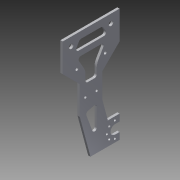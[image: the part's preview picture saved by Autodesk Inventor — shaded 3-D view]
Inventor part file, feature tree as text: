
AUTODESK INVENTOR PART (.ipt)
format: ipt  version: 2013 (Build 170138000, 138)  size: 268,288 bytes
history: native  units: mm
features: sketch x8, extrude x6, fillet x3, hole x2, other x1, pattern_circular x1
ambient origin geometry x8: Origin, YZ Plane, XZ Plane, XY Plane, X Axis, Y Axis, Z Axis, Center Point
feature tree (21):
  other  "ソリッド1"
  extrude  "押し出し1"  Depth=50.0mm
  extrude  "押し出し2"  Depth=100.0mm
  extrude  "押し出し5"  Depth=50.0mm
  hole  "穴1"  [1 undecoded]
  pattern_circular  "円形状パターン2"  [2 undecoded]
  hole  "穴2"  [1 undecoded]
  extrude  "押し出し7"  TaperAngle=135.0deg  [1 undecoded]
  extrude  "押し出し8"  Depth=25.0mm
  fillet  "フィレット1"  Radius=25.0mm
  fillet  "フィレット2"  Radius=50.0mm
  extrude  "押し出し9"  TaperAngle=165.0deg  [1 undecoded]
  fillet  "フィレット3"  Radius=20.0mm
  sketch  "スケッチ1"
  sketch  "スケッチ2"
  sketch  "スケッチ3"
  sketch  "スケッチ4"
  sketch  "スケッチ5"
  sketch  "スケッチ7"
  sketch  "スケッチ8"
  sketch  "スケッチ10"
note: 6 required parameter values undecoded (feature->parameter linkage not recoverable at this tier; creation-order binding heuristic only, values carry confidence <= 0.55)
